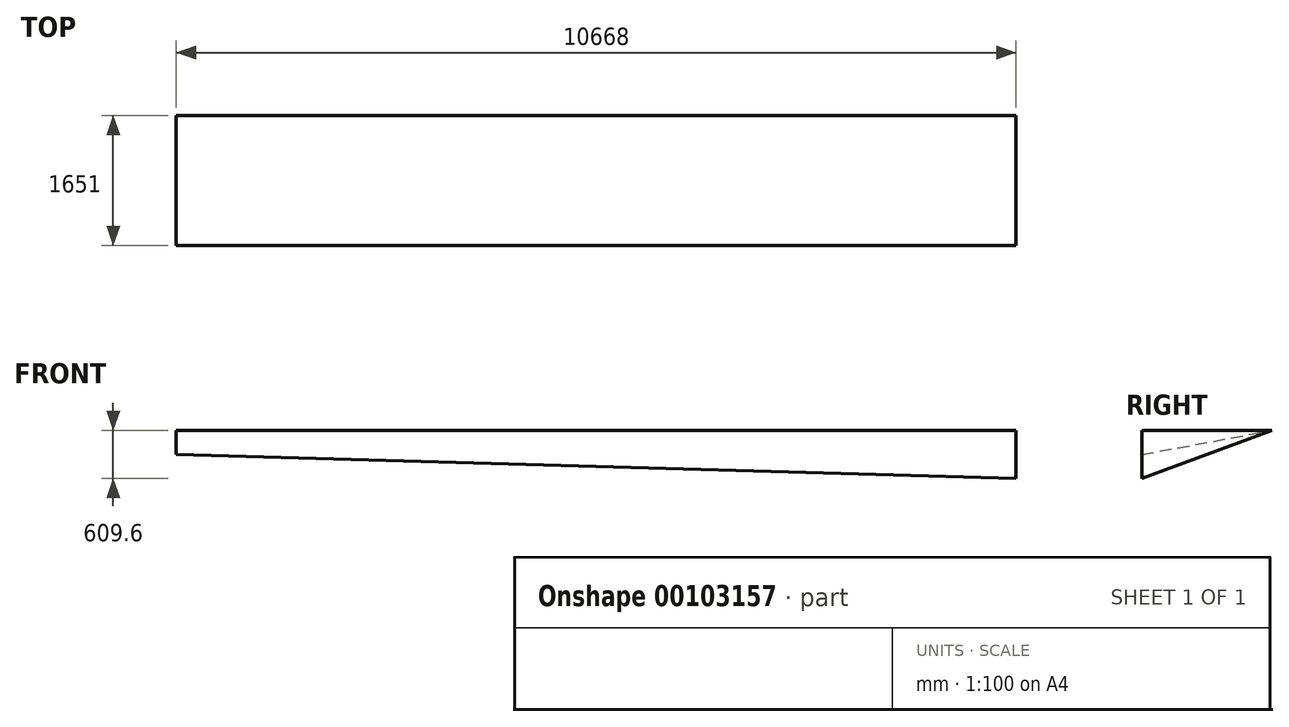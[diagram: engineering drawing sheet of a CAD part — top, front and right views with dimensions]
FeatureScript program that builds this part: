
annotation { "Feature Type Name" : "Feature", "Feature Type Description" : "" }
export const myFeature = defineFeature(function(context is Context, id is Id, definition is map)
    precondition{}
    {
        {
            var Q0;
            Q0=qCreatedBy(makeId("Right.planeOp"),FACE);
            var sketch = newSketch(context, id + "F0", { "sketchPlane" : qUnion([Q0])});
            skLineSegment(sketch, "E0", {"start": v(0, 0) * mm, "end": v(0, -304.8) * mm});
            skLineSegment(sketch, "E1", {"start": v(0, -304.8) * mm, "end": v(1651, 0) * mm});
            skLineSegment(sketch, "E2", {"start": v(1651, 0) * mm, "end": v(0, 0) * mm});
            skSolve(sketch);
        }
        {
            var Q0;
            Q0=qCreatedBy(makeId("Right.planeOp"),FACE);
            cPlane(context, id + "F1", {"entities" : qUnion([Q0]), "cplaneType" : CPlaneType.OFFSET, "offset" : 10668 * mm, "width" : 152.4 * mm, "height" : 152.4 * mm});
        }
        {
            var Q0;
            Q0=qCreatedBy(id+"F1.planeOp",FACE);
            var sketch = newSketch(context, id + "F2", { "sketchPlane" : qUnion([Q0])});
            skLineSegment(sketch, "E3", {"start": v(0, 0) * mm, "end": v(0, -609.6) * mm});
            skLineSegment(sketch, "E4", {"start": v(0, -609.6) * mm, "end": v(1651, 0) * mm});
            skLineSegment(sketch, "E5", {"start": v(1651, 0) * mm, "end": v(0, 0) * mm});
            skSolve(sketch);
        }
        {
            var Q0;
            Q0 = qSketchRegion(id + "F0", true);
            var Q1;
            Q1 = qSketchRegion(id + "F2", true);
            loft(context, id + "F3", {"sheetProfilesArray" : [{ "sheetProfileEntities" : qUnion([Q0]) }, { "sheetProfileEntities" : qUnion([Q1]) }]});
        }
    });
